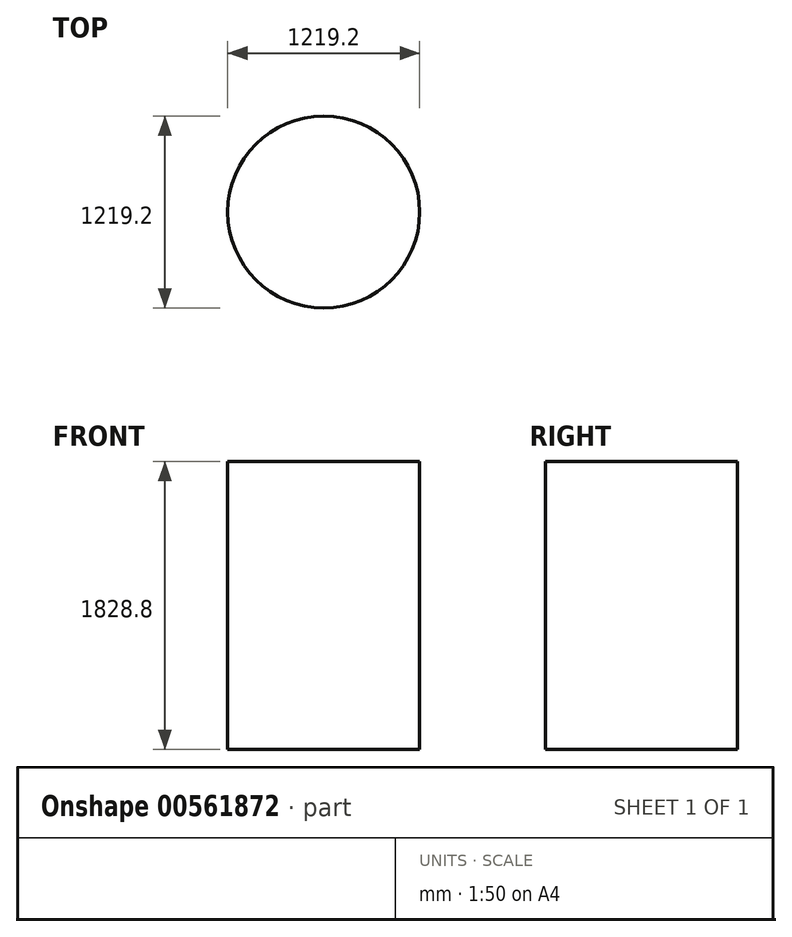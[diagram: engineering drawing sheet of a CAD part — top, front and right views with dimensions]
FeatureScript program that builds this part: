
annotation { "Feature Type Name" : "Feature", "Feature Type Description" : "" }
export const myFeature = defineFeature(function(context is Context, id is Id, definition is map)
    precondition{}
    {
        {
            var Q0;
            Q0=qCreatedBy(makeId("Top.planeOp"),FACE);
            var sketch = newSketch(context, id + "F0", { "sketchPlane" : qUnion([Q0])});
            skCircle(sketch, "E0", {"center": v(0, 0) * mm, "radius": 609.6 * mm});
            skSolve(sketch);
        }
        {
            var Q0;
            Q0=makeQuery(id+"F0.imprint","IMPRINT",FACE,{"disambiguationData":[TD([[makeQuery(id+"F0.imprint","IMPRINT",EDGE,{"derivedFrom":sQuery(id+"F0.wireOp",EDGE,"E0")}),1.0]])]});
            extrude(context, id + "F1", {"entities" : qUnion([Q0]), "endBound" : BoundingType.SYMMETRIC, "depth" : 1828.8 * mm, "offsetDistance" : 25.4 * mm});
        }
    });
